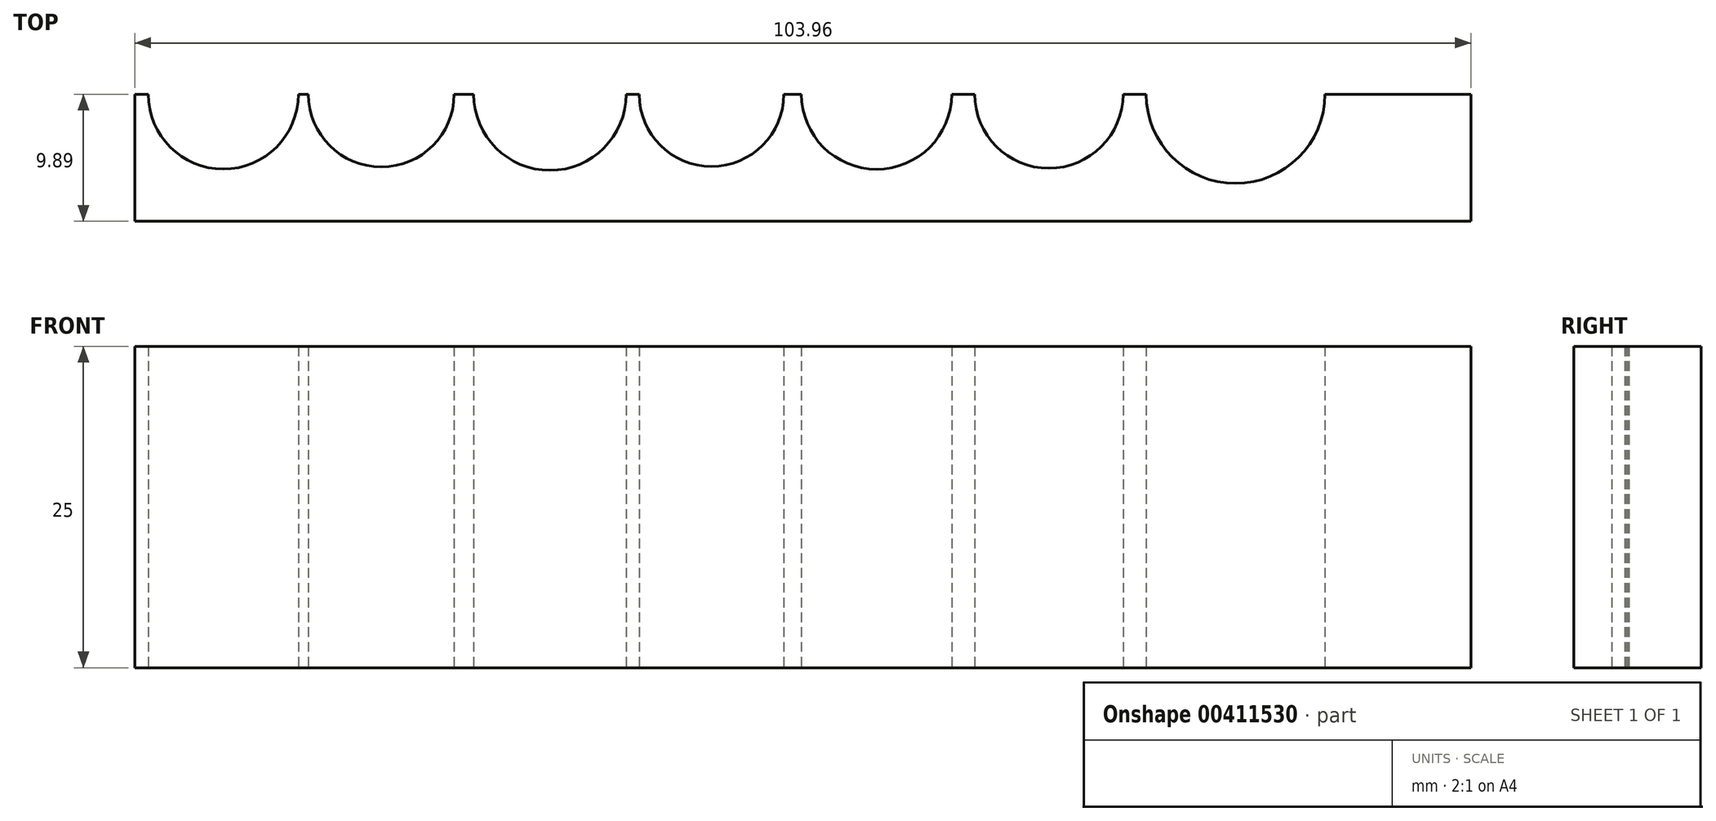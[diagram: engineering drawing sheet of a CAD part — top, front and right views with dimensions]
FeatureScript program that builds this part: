
annotation { "Feature Type Name" : "Feature", "Feature Type Description" : "" }
export const myFeature = defineFeature(function(context is Context, id is Id, definition is map)
    precondition{}
    {
        {
            var Q0;
            Q0=qCreatedBy(makeId("Top.planeOp"),FACE);
            var sketch = newSketch(context, id + "F0", { "sketchPlane" : qUnion([Q0])});
            skLineSegment(sketch, "E0.bottom", {"start": v(-51.98, 9.89) * mm, "end": v(51.98, 9.89) * mm});
            skLineSegment(sketch, "E0.top", {"start": v(-51.98, -9.89) * mm, "end": v(51.98, -9.89) * mm});
            skLineSegment(sketch, "E0.left", {"start": v(-51.98, 9.89) * mm, "end": v(-51.98, -9.89) * mm});
            skLineSegment(sketch, "E0.right", {"start": v(51.98, 9.89) * mm, "end": v(51.98, -9.89) * mm});
            skPoint(sketch, "E0.middle", {"position": v(0, 0) * mm});
            skSolve(sketch);
        }
        {
            var Q0;
            Q0 = qSketchRegion(id + "F0", true);
            extrude(context, id + "F1", {"entities" : qUnion([Q0]), "depth" : 25 * mm, "offsetDistance" : 25 * mm});
        }
        {
            var Q0;
            Q0=qCreatedBy(makeId("Top.planeOp"),FACE);
            var sketch = newSketch(context, id + "F2", { "sketchPlane" : qUnion([Q0])});
            skCircle(sketch, "E1", {"center": v(-45.1, 0) * mm, "radius": 5.84 * mm});
            skCircle(sketch, "E2", {"center": v(-32.81, 0) * mm, "radius": 5.67 * mm});
            skCircle(sketch, "E3", {"center": v(-19.69, 0) * mm, "radius": 5.93 * mm});
            skCircle(sketch, "E4", {"center": v(-7.12, 0) * mm, "radius": 5.63 * mm});
            skCircle(sketch, "E5", {"center": v(5.72, 0) * mm, "radius": 5.85 * mm});
            skCircle(sketch, "E6", {"center": v(19.13, 0) * mm, "radius": 5.77 * mm});
            skCircle(sketch, "E7", {"center": v(33.65, 0) * mm, "radius": 6.95 * mm});
            skSolve(sketch);
        }
        {
            var Q0;
            Q0 = qSketchRegion(id + "F2", true);
            extrude(context, id + "F3", {"entities" : qUnion([Q0]), "operationType" : NewBodyOperationType.REMOVE, "depth" : 25 * mm, "offsetDistance" : 25 * mm});
        }
        {
            var Q0;
            Q0=qCreatedBy(makeId("Top.planeOp"),FACE);
            var sketch = newSketch(context, id + "F4", { "sketchPlane" : qUnion([Q0])});
            skLineSegment(sketch, "E8.bottom", {"start": v(-52.94, 0) * mm, "end": v(57.04, 0) * mm});
            skLineSegment(sketch, "E8.top", {"start": v(-52.94, 10.37) * mm, "end": v(57.04, 10.37) * mm});
            skLineSegment(sketch, "E8.left", {"start": v(-52.94, 0) * mm, "end": v(-52.94, 10.37) * mm});
            skLineSegment(sketch, "E8.right", {"start": v(57.04, 0) * mm, "end": v(57.04, 10.37) * mm});
            skSolve(sketch);
        }
        {
            var Q0;
            Q0 = qSketchRegion(id + "F4", true);
            extrude(context, id + "F5", {"entities" : qUnion([Q0]), "operationType" : NewBodyOperationType.REMOVE, "depth" : 25 * mm, "offsetDistance" : 25 * mm});
        }
    });
